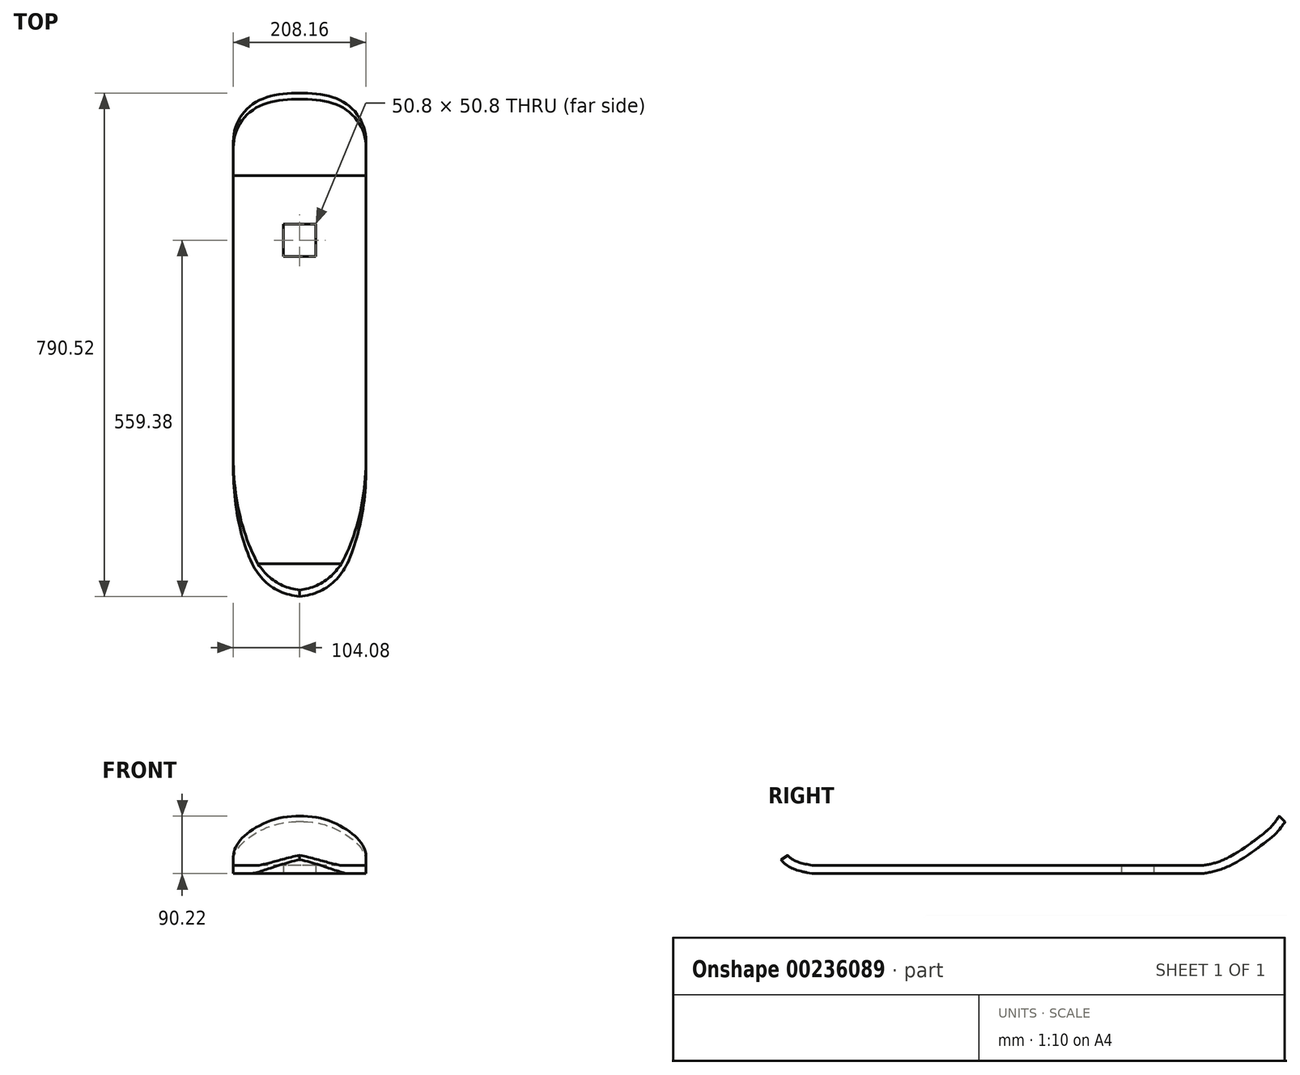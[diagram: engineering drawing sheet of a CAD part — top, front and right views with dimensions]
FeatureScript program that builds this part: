
annotation { "Feature Type Name" : "Feature", "Feature Type Description" : "" }
export const myFeature = defineFeature(function(context is Context, id is Id, definition is map)
    precondition{}
    {
        {
            var Q0;
            Q0=qCreatedBy(makeId("Top.planeOp"),FACE);
            var sketch = newSketch(context, id + "F0", { "sketchPlane" : qUnion([Q0])});
            skLineSegment(sketch, "E0.bottom", {"start": v(104.08, -304.8) * mm, "end": v(-104.08, -304.8) * mm});
            skLineSegment(sketch, "E0.top", {"start": v(104.08, 304.8) * mm, "end": v(-104.08, 304.8) * mm});
            skLineSegment(sketch, "E0.left", {"start": v(104.08, -304.8) * mm, "end": v(104.08, 304.8) * mm});
            skLineSegment(sketch, "E0.right", {"start": v(-104.08, -304.8) * mm, "end": v(-104.08, 304.8) * mm});
            skPoint(sketch, "E0.middle", {"position": v(0, 0) * mm});
            skLineSegment(sketch, "E1.bottom", {"start": v(25.4, 177.8) * mm, "end": v(-25.4, 177.8) * mm});
            skLineSegment(sketch, "E1.top", {"start": v(25.4, 228.6) * mm, "end": v(-25.4, 228.6) * mm});
            skLineSegment(sketch, "E1.left", {"start": v(25.4, 177.8) * mm, "end": v(25.4, 228.6) * mm});
            skLineSegment(sketch, "E1.right", {"start": v(-25.4, 177.8) * mm, "end": v(-25.4, 228.6) * mm});
            skPoint(sketch, "E1.middle", {"position": v(0, 203.2) * mm});
            skSolve(sketch);
        }
        {
            var Q0;
            Q0 = qSketchRegion(id + "F0", true);
            extrude(context, id + "F1", {"entities" : qUnion([Q0]), "endBound" : BoundingType.SYMMETRIC, "depth" : 12.7 * mm});
        }
        {
            var Q0;
            Q0=qCreatedBy(makeId("Right.planeOp"),FACE);
            var sketch = newSketch(context, id + "F2", { "sketchPlane" : qUnion([Q0])});
            skFitSpline(sketch, "E2", {"points": [v(305.2, 0) * mm, v(333.1, 6.72) * mm, v(366.77, 24.09) * mm, v(386.25, 37.77) * mm, v(415.72, 61.45) * mm, v(429.93, 79.87) * mm], "startDerivative": vector(137, 22.96) * mm, "endDerivative": vector(66.25, 102.06) * mm});
            skSolve(sketch);
        }
        {
            var Q0;
            Q0=makeQuery(id+"F1.opExtrude","SWEPT_FACE",FACE,{"disambiguationData":[OSD([sQuery(id+"F0.wireOp",EDGE,"E0.top")])]});
            var Q1;
            Q1=sQuery(id+"F2.wireOp",EDGE,"E2");
            sweep(context, id + "F3", {"operationType" : NewBodyOperationType.ADD, "profiles" : qUnion([Q0]), "path" : qUnion([Q1])});
        }
        {
            var Q0;
            Q0=qCreatedBy(makeId("Right.planeOp"),FACE);
            var sketch = newSketch(context, id + "F4", { "sketchPlane" : qUnion([Q0])});
            skFitSpline(sketch, "E3", {"points": [v(-304.98, 0) * mm, v(-329.88, 5.24) * mm, v(-347.66, 14.9) * mm, v(-352.74, 22.52) * mm], "startDerivative": vector(-63.12, 9.51) * mm, "endDerivative": vector(-15.55, 31.96) * mm});
            skSolve(sketch);
        }
        {
            var Q0;
            Q0=makeQuery(id+"F1.opExtrude","SWEPT_FACE",FACE,{"disambiguationData":[OSD([sQuery(id+"F0.wireOp",EDGE,"E0.bottom")])]});
            var Q1;
            Q1=sQuery(id+"F4.wireOp",EDGE,"E3");
            sweep(context, id + "F5", {"operationType" : NewBodyOperationType.ADD, "profiles" : qUnion([Q0]), "path" : qUnion([Q1])});
        }
        {
            var Q0;
            Q0=makeQuery(id+"F5.opSweep","CAP_EDGE",EDGE,{"disambiguationData":[OSD([sQuery(id+"F0.wireOp",EDGE,"E0.bottom"),sQuery(id+"F0.wireOp",EDGE,"E0.left"),sQuery(id+"F4.wireOp",VERTEX,"E3.end")])],"isStart":false});
            var Q1;
            Q1=makeQuery(id+"F5.opSweep","CAP_EDGE",EDGE,{"disambiguationData":[OSD([sQuery(id+"F0.wireOp",EDGE,"E0.bottom"),sQuery(id+"F0.wireOp",EDGE,"E0.right"),sQuery(id+"F4.wireOp",VERTEX,"E3.end")])],"isStart":false});
            fillet(context, id + "F6", {"entities" : qUnion([Q0, Q1]), "radius" : 134.9 * mm, "tangentPropagation" : true, "allowEdgeOverflow" : false});
        }
        {
            var Q0;
            Q0=makeQuery(id+"F3.opSweep","CAP_EDGE",EDGE,{"disambiguationData":[OSD([sQuery(id+"F0.wireOp",EDGE,"E0.top"),sQuery(id+"F0.wireOp",EDGE,"E0.left"),sQuery(id+"F2.wireOp",VERTEX,"E2.end")])],"isStart":false});
            var Q1;
            Q1=makeQuery(id+"F3.opSweep","CAP_EDGE",EDGE,{"disambiguationData":[OSD([sQuery(id+"F0.wireOp",EDGE,"E0.top"),sQuery(id+"F0.wireOp",EDGE,"E0.right"),sQuery(id+"F2.wireOp",VERTEX,"E2.end")])],"isStart":false});
            fillet(context, id + "F7", {"entities" : qUnion([Q0, Q1]), "radius" : 98.11 * mm, "tangentPropagation" : true, "allowEdgeOverflow" : false});
        }
    });
